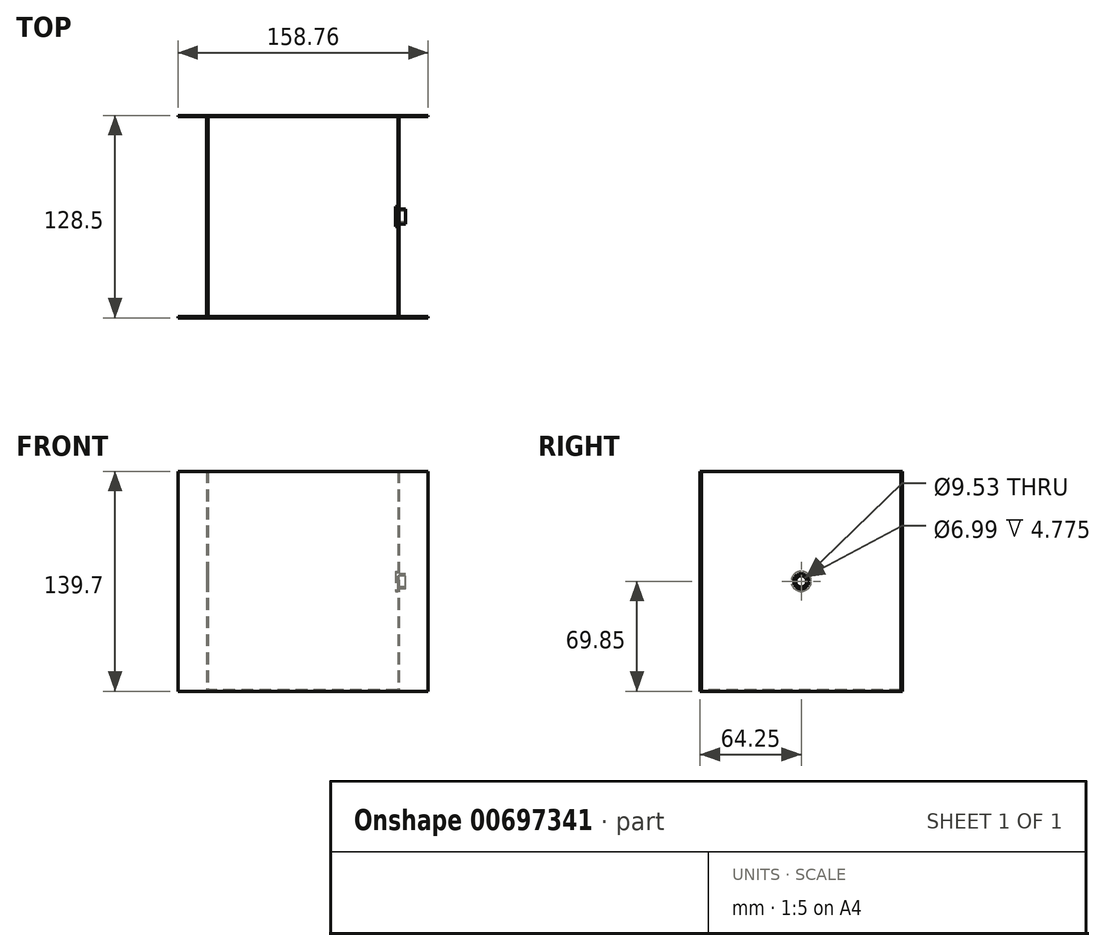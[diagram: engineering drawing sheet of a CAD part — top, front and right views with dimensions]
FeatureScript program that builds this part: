
annotation { "Feature Type Name" : "Feature", "Feature Type Description" : "" }
export const myFeature = defineFeature(function(context is Context, id is Id, definition is map)
    precondition{}
    {
        {
            assignVariable(context, id + "F0", {"name" : "Thickness", "anyValue" : 0.75});
        }
        {
            var Q0;
            Q0=qCreatedBy(makeId("Top.planeOp"),FACE);
            var sketch = newSketch(context, id + "F1", { "sketchPlane" : qUnion([Q0])});
            skLineSegment(sketch, "E0.bottom", {"start": v(60.32, 63.5) * mm, "end": v(-60.33, 63.5) * mm});
            skLineSegment(sketch, "E0.top", {"start": v(60.33, -63.5) * mm, "end": v(-60.32, -63.5) * mm});
            skLineSegment(sketch, "E0.left", {"start": v(60.32, 63.5) * mm, "end": v(60.33, -63.5) * mm});
            skLineSegment(sketch, "E0.right", {"start": v(-60.33, 63.5) * mm, "end": v(-60.32, -63.5) * mm});
            skPoint(sketch, "E0.middle", {"position": v(0, 0) * mm});
            skSolve(sketch);
        }
        {
            var Q0;
            Q0=makeQuery(id+"F1.imprint","IMPRINT",FACE,{"disambiguationData":[TD([[makeQuery(id+"F1.imprint","IMPRINT",EDGE,{"derivedFrom":sQuery(id+"F1.wireOp",EDGE,"E0.bottom")}),1.0]])]});
            extrude(context, id + "F2", {"entities" : qUnion([Q0]), "depth" : (getVariable(context, 'Thickness')) * mm, "offsetDistance" : 25.4 * mm});
        }
        {
            var Q0;
            Q0=makeQuery(id+"F2.opExtrude","SWEPT_FACE",FACE,{"disambiguationData":[OSD([sQuery(id+"F1.wireOp",EDGE,"E0.right")])]});
            var sketch = newSketch(context, id + "F3", { "sketchPlane" : qUnion([Q0])});
            skLineSegment(sketch, "E1.bottom", {"start": v(-63.5, 0) * mm, "end": v(63.5, 0) * mm});
            skLineSegment(sketch, "E1.top", {"start": v(-63.5, 139.7) * mm, "end": v(63.5, 139.7) * mm});
            skLineSegment(sketch, "E1.left", {"start": v(-63.5, 0) * mm, "end": v(-63.5, 139.7) * mm});
            skLineSegment(sketch, "E1.right", {"start": v(63.5, 0) * mm, "end": v(63.5, 139.7) * mm});
            skSolve(sketch);
        }
        {
            var Q0;
            Q0 = qSketchRegion(id + "F3", true);
            extrude(context, id + "F4", {"entities" : qUnion([Q0]), "depth" : (getVariable(context, 'Thickness')) * mm, "offsetDistance" : 25.4 * mm});
        }
        {
            var Q0;
            Q0=makeQuery(id+"F4.opExtrude","CAP_FACE",FACE,{"disambiguationData":[OSD([sQuery(id+"F3.wireOp",EDGE,"E1.bottom"),sQuery(id+"F3.wireOp",EDGE,"E1.top"),sQuery(id+"F3.wireOp",EDGE,"E1.left"),sQuery(id+"F3.wireOp",EDGE,"E1.right")])],"isStart":false});
            var sketch = newSketch(context, id + "F5", { "sketchPlane" : qUnion([Q0])});
            skCircle(sketch, "E2", {"center": v(0, 69.85) * mm, "radius": 4.76 * mm});
            skPoint(sketch, "E2.centerSnap0", {"position": v(63.5, 69.85) * mm});
            skSolve(sketch);
        }
        {
            var Q0;
            Q0 = qSketchRegion(id + "F5", true);
            extrude(context, id + "F6", {"entities" : qUnion([Q0]), "operationType" : NewBodyOperationType.REMOVE, "endBound" : BoundingType.THROUGH_ALL, "oppositeDirection" : true, "depth" : 25.4 * mm, "offsetDistance" : 25.4 * mm});
        }
        {
            var Q0;
            Q0=makeQuery(id+"F4.opExtrude","SWEPT_BODY",BODY,{"disambiguationData":[OSD([sQuery(id+"F3.wireOp",EDGE,"E1.bottom"),sQuery(id+"F3.wireOp",EDGE,"E1.top"),sQuery(id+"F3.wireOp",EDGE,"E1.left"),sQuery(id+"F3.wireOp",EDGE,"E1.right")])]});
            var Q1;
            Q1=qCreatedBy(makeId("Right.planeOp"),FACE);
            mirror(context, id + "F7", {"entities" : qUnion([Q0]), "mirrorPlane" : qUnion([Q1])});
        }
        {
            var Q0;
            Q0=makeQuery(id+"F4.opExtrude","SWEPT_FACE",FACE,{"disambiguationData":[OSD([sQuery(id+"F3.wireOp",EDGE,"E1.left")])]});
            var sketch = newSketch(context, id + "F8", { "sketchPlane" : qUnion([Q0])});
            skLineSegment(sketch, "E3.bottom", {"start": v(79.38, 0) * mm, "end": v(-79.38, 0) * mm});
            skLineSegment(sketch, "E3.top", {"start": v(79.37, 139.7) * mm, "end": v(-79.38, 139.7) * mm});
            skLineSegment(sketch, "E3.left", {"start": v(79.38, 0) * mm, "end": v(79.37, 139.7) * mm});
            skLineSegment(sketch, "E3.right", {"start": v(-79.38, 0) * mm, "end": v(-79.38, 139.7) * mm});
            skSolve(sketch);
        }
        {
            var Q0;
            Q0 = qSketchRegion(id + "F8", true);
            extrude(context, id + "F9", {"entities" : qUnion([Q0]), "depth" : (getVariable(context, 'Thickness')) * mm, "offsetDistance" : 25.4 * mm});
        }
        {
            var Q0;
            Q0=makeQuery(id+"F9.opExtrude","SWEPT_BODY",BODY,{"disambiguationData":[OSD([sQuery(id+"F8.wireOp",EDGE,"E3.bottom"),sQuery(id+"F8.wireOp",EDGE,"E3.top"),sQuery(id+"F8.wireOp",EDGE,"E3.left"),sQuery(id+"F8.wireOp",EDGE,"E3.right")])]});
            var Q1;
            Q1=qCreatedBy(makeId("Front.planeOp"),FACE);
            mirror(context, id + "F10", {"entities" : qUnion([Q0]), "mirrorPlane" : qUnion([Q1])});
        }
        {
            var Q0;
            Q0=makeQuery(id+"F7.opPattern","COPY",FACE,{"derivedFrom":makeQuery(id+"F4.opExtrude","CAP_FACE",FACE,{"disambiguationData":[OSD([sQuery(id+"F3.wireOp",EDGE,"E1.bottom"),sQuery(id+"F3.wireOp",EDGE,"E1.top"),sQuery(id+"F3.wireOp",EDGE,"E1.left"),sQuery(id+"F3.wireOp",EDGE,"E1.right")])],"isStart":true}),"instanceName":"1"});
            var sketch = newSketch(context, id + "F11", { "sketchPlane" : qUnion([Q0])});
            skCircle(sketch, "E4", {"center": v(0, 69.85) * mm, "radius": 6.35 * mm});
            skSolve(sketch);
        }
        {
            var Q0;
            Q0 = qSketchRegion(id + "F11", true);
            extrude(context, id + "F12", {"entities" : qUnion([Q0]), "depth" : 1.63 * mm, "offsetDistance" : 25.4 * mm});
        }
        {
            var Q0;
            Q0=makeQuery(id+"F12.opExtrude","CAP_FACE",FACE,{"disambiguationData":[OSD([sQuery(id+"F11.wireOp",EDGE,"E4")])],"isStart":true});
            var sketch = newSketch(context, id + "F13", { "sketchPlane" : qUnion([Q0])});
            skCircle(sketch, "E5.0", {"center": v(0, 69.85) * mm, "radius": 4.76 * mm});
            skCircle(sketch, "E6.0", {"center": v(0, 69.85) * mm, "radius": 3.5 * mm});
            skSolve(sketch);
        }
        {
            var Q0;
            Q0=makeQuery(id+"F13.imprint","IMPRINT",FACE,{"disambiguationData":[TD([[makeQuery(id+"F13.imprint","IMPRINT",EDGE,{"derivedFrom":sQuery(id+"F13.wireOp",EDGE,"E5.0")}),1.0]])]});
            extrude(context, id + "F14", {"entities" : qUnion([Q0]), "operationType" : NewBodyOperationType.ADD, "depth" : 4.78 * mm, "offsetDistance" : 25.4 * mm});
        }
    });
